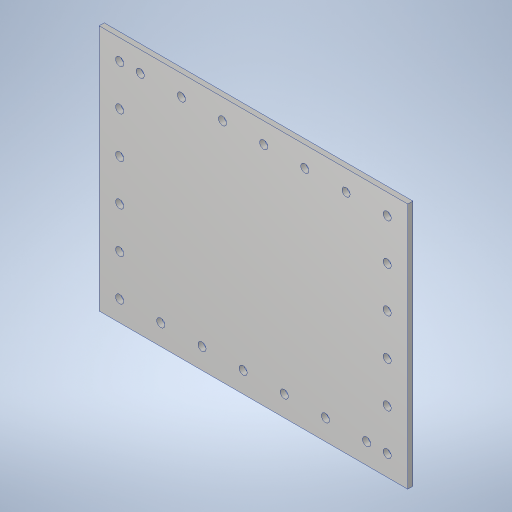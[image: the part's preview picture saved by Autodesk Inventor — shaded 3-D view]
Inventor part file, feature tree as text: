
AUTODESK INVENTOR PART (.ipt)
format: ipt  version: 2023.4 (Build 274418000, 418)  size: 266,240 bytes
history: native  units: in
note: dims shown in document units (in); Inventor stores cm internally (conversion verified against a paired STEP export)
features: pattern_linear x4, hole x2, extrude x1, sketch x1, projected_geometry x1
ambient origin geometry x8: Origin, YZ Plane, XZ Plane, XY Plane, X Axis, Y Axis, Z Axis, Center Point
bodies: Solid1 (feature_tree)
feature tree (9):
  extrude  "Extrusion1"  Depth=0.5in
  sketch  "Sketch2"  dims[d3=0.0in d4=0.5in d5=0.5in d6=0.201in d7=0.75in d8=0.385in d9=0.25in d10=0.5635in d11=1.0in d12=0.8108in d13=3.1496in d15=1.0in d16=2.7559in d18=1.0in d19=0.5in d20=0.5in d21=0.201in d22=0.75in d23=0.375in d24=0.25in d25=0.5635in d26=1.0in d27=0.8108in d28=2.7559in d30=1.0in d31=2.7559in d33=1.0in]
  hole  "Hole1"  [1 undecoded]
  pattern_linear  "Rectangular Pattern1"  Count1=8 Spacing1=1.0in
  pattern_linear  "Rectangular Pattern2"  Count1=7 Spacing1=1.0in
  hole  "Hole2"  [1 undecoded]
  pattern_linear  "Rectangular Pattern3"  Spacing1=0.5in  [1 undecoded]
  pattern_linear  "Rectangular Pattern4"  Count1=7 Spacing1=1.0in
  projected_geometry  "Project Cut Edges1"
note: 3 required parameter values undecoded (feature->parameter linkage not recoverable at this tier; creation-order binding heuristic only, values carry confidence <= 0.55)
